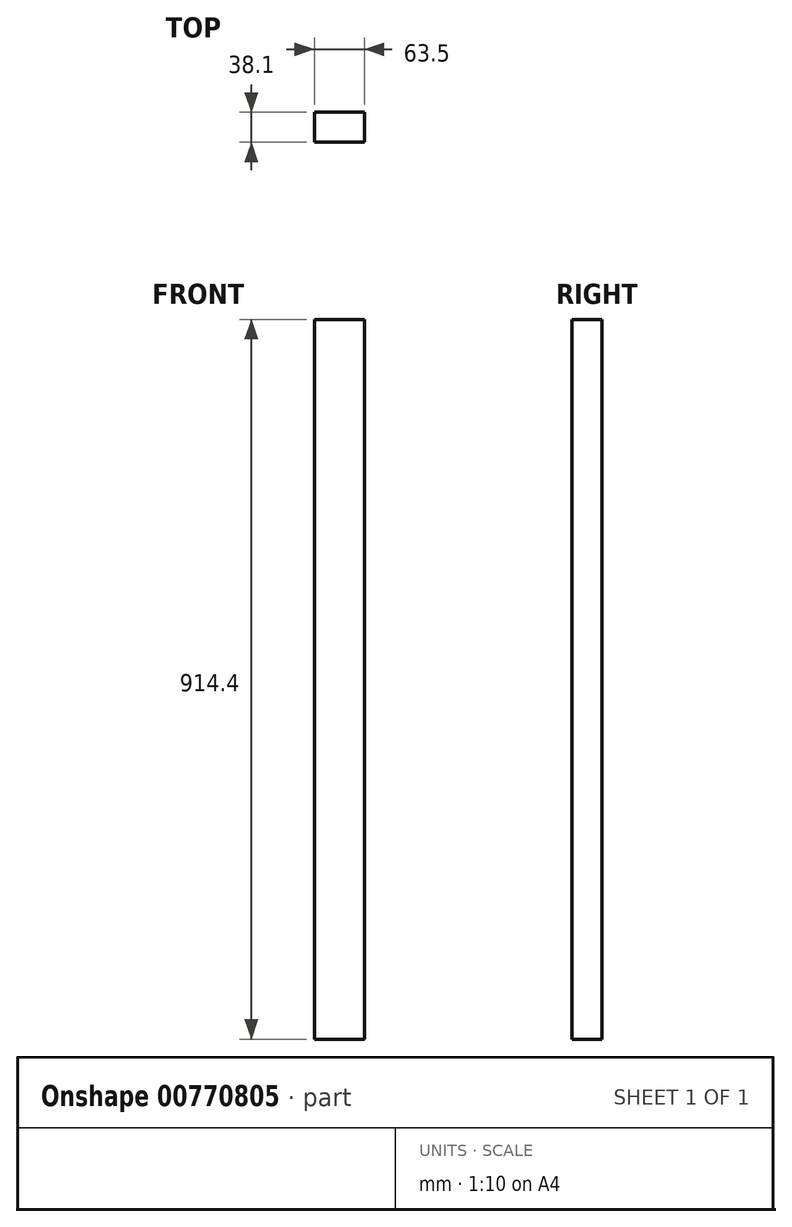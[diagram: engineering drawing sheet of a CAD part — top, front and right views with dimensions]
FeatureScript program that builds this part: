
annotation { "Feature Type Name" : "Feature", "Feature Type Description" : "" }
export const myFeature = defineFeature(function(context is Context, id is Id, definition is map)
    precondition{}
    {
        {
            var Q0;
            Q0=qCreatedBy(makeId("Top.planeOp"),FACE);
            var sketch = newSketch(context, id + "F0", { "sketchPlane" : qUnion([Q0])});
            skLineSegment(sketch, "E0.bottom", {"start": v(0, 0) * mm, "end": v(63.5, 0) * mm});
            skLineSegment(sketch, "E0.top", {"start": v(0, 38.1) * mm, "end": v(63.5, 38.1) * mm});
            skLineSegment(sketch, "E0.left", {"start": v(0, 0) * mm, "end": v(0, 38.1) * mm});
            skLineSegment(sketch, "E0.right", {"start": v(63.5, 0) * mm, "end": v(63.5, 38.1) * mm});
            skSolve(sketch);
        }
        {
            var Q0;
            Q0=makeQuery(id+"F0.imprint","IMPRINT",FACE,{"disambiguationData":[TD([[makeQuery(id+"F0.imprint","IMPRINT",EDGE,{"derivedFrom":sQuery(id+"F0.wireOp",EDGE,"E0.bottom")}),1.0]])]});
            extrude(context, id + "F1", {"entities" : qUnion([Q0]), "oppositeDirection" : true, "depth" : 914.4 * mm, "offsetDistance" : 25.4 * mm});
        }
    });
